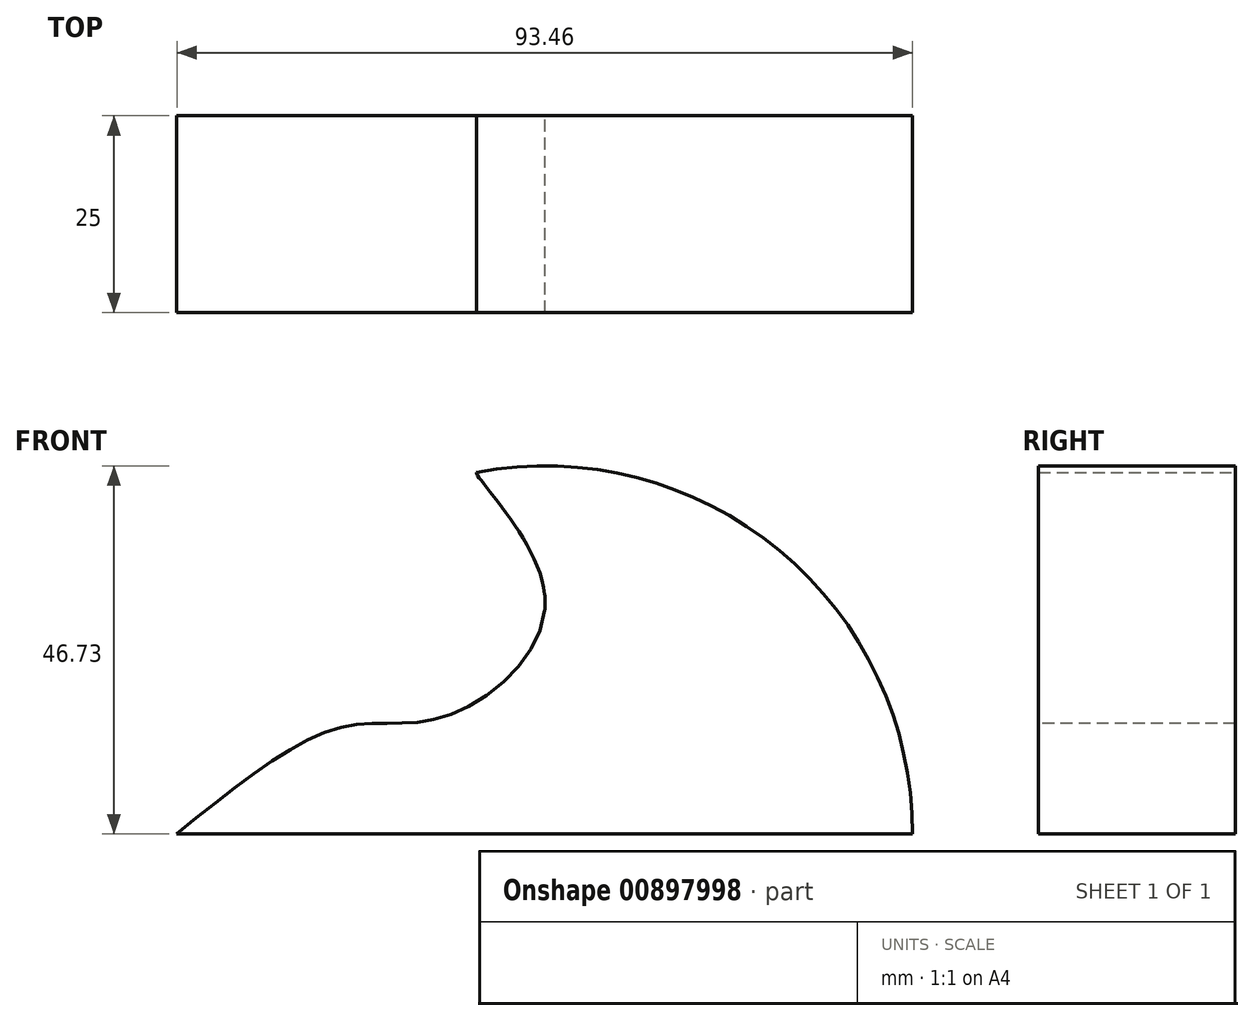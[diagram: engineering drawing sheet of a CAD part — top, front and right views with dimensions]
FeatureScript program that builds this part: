
annotation { "Feature Type Name" : "Feature", "Feature Type Description" : "" }
export const myFeature = defineFeature(function(context is Context, id is Id, definition is map)
    precondition{}
    {
        {
            var Q0;
            Q0=qCreatedBy(makeId("Front.planeOp"),FACE);
            var sketch = newSketch(context, id + "F0", { "sketchPlane" : qUnion([Q0])});
            skCircle(sketch, "E0", {"center": v(0, 0) * mm, "radius": 46.73 * mm});
            skLineSegment(sketch, "E1", {"start": v(-46.73, 0) * mm, "end": v(46.73, 0) * mm});
            skLineSegment(sketch, "E2", {"start": v(0, 46.73) * mm, "end": v(0, -46.73) * mm});
            skFitSpline(sketch, "E3", {"points": [v(-46.73, 0) * mm, v(-25.71, 13.58) * mm, v(-12.77, 14.88) * mm, v(0, 30.4) * mm, v(-8.68, 45.92) * mm, v(-8.17, 46.01) * mm], "startDerivative": vector(80.46, 65.41) * mm, "endDerivative": vector(18.43, -1.94) * mm});
            skFitSpline(sketch, "E4", {"points": [v(-27.54, -37.76) * mm, v(0, -25.87) * mm, v(19.57, -30.4) * mm, v(36.38, -19.4) * mm, v(41.16, -22.12) * mm], "startDerivative": vector(87.5, 58.18) * mm, "endDerivative": vector(29.03, -34.23) * mm});
            skFitSpline(sketch, "E5", {"points": [v(23.08, 40.64) * mm, v(8.57, 17.46) * mm, v(22.15, 11.64) * mm, v(35.09, 2.59) * mm, v(46.73, 0) * mm], "startDerivative": vector(-77.94, -89.34) * mm, "endDerivative": vector(57.89, -4.5) * mm});
            skSolve(sketch);
        }
        {
            var Q0;
            {var subQ0=sQuery(id+"F0.wireOp",EDGE,"E2");var subQ1=sQuery(id+"F0.wireOp",EDGE,"E0");var subQ2=makeQuery(id+"F0.imprint","INTERSECT",VERTEX,{"disambiguationData":[OD(1.0)],"derivedFrom":[subQ1,subQ0]});Q0=makeQuery(id+"F0.imprint","IMPRINT",FACE,{"disambiguationData":[TD([[makeQuery(id+"F0.imprint","IMPRINT",EDGE,{"disambiguationData":[TD([[subQ2,-1.0]])],"derivedFrom":subQ1}),1.0]])]});}
            var Q1;
            {var subQ0=sQuery(id+"F0.wireOp",EDGE,"E2");var subQ1=sQuery(id+"F0.wireOp",EDGE,"E0");var subQ2=makeQuery(id+"F0.imprint","INTERSECT",VERTEX,{"disambiguationData":[OD(1.0)],"derivedFrom":[subQ1,subQ0]});Q1=makeQuery(id+"F0.imprint","IMPRINT",FACE,{"disambiguationData":[TD([[makeQuery(id+"F0.imprint","IMPRINT",EDGE,{"disambiguationData":[TD([[subQ2,1.0]])],"derivedFrom":subQ1}),1.0]])]});}
            var Q2;
            {var subQ0=sQuery(id+"F0.wireOp",EDGE,"E5");Q2=makeQuery(id+"F0.imprint","IMPRINT",FACE,{"disambiguationData":[TD([[makeQuery(id+"F0.imprint","IMPRINT",EDGE,{"derivedFrom":subQ0}),1.0]])]});}
            var Q3;
            {var subQ0=sQuery(id+"F0.wireOp",EDGE,"E3");var subQ4=sQuery(id+"F0.wireOp",EDGE,"E2");var subQ5=makeQuery(id+"F0.imprint","INTERSECT",VERTEX,{"disambiguationData":[OD(0.0)],"derivedFrom":[subQ4,subQ0]});Q3=makeQuery(id+"F0.imprint","IMPRINT",FACE,{"disambiguationData":[TD([[makeQuery(id+"F0.imprint","IMPRINT",EDGE,{"disambiguationData":[TD([[subQ5,-1.0]])],"derivedFrom":subQ4}),-1.0]])]});}
            extrude(context, id + "F1", {"entities" : qUnion([Q0, Q1, Q2, Q3]), "depth" : 25 * mm, "offsetDistance" : 25 * mm});
        }
    });
